# Revit family: flat_polymero_kreis_311610_002_8_19_0b9d
name_source: partatom
category: Lighting Fixtures
units: mm (PartAtom-declared; Revit-internal decimal feet)

## family parameters
Cut with Voids When Loaded = No
Host = Face
Light Source = No
Part Type = Normal
Room Calculation Point = No
Round Connector Dimension = Use Diameter
Shared = No

## types (1)
- FLAT POLYMERO KREIS (1 x LED Modul 830, 1650 lm, 3000)
    Apparent Load = 14 VA
    CIE Flux Codes = 42 73 92 86 100
    Color Rendering = 80
    Color Temperature = 3000
    Default Elevation = 1800 mm
    Description = Series: FLAT POLYMERO KREIS
Decorative round surface-mounted luminaire. Base: metal, powder-coated. Diffuser made of plastic (polycarbonate), opal, shockproof. Diffuser fastening: patented push system. Suitable for Ceiling mounting, Wall (surface). With integrated HF movement sensor. Functional parameters of the motion detector (ceiling mounting up to 4.0 m or wall mounting up to 2.7 m): HF detector 5.8 GHz ISM frequency band. Sensitivity/Range: 1-8 m in diameter, adjustable from 20-100%. Time control between 10 seconds and 30 minutes, adjustable. Coverage: 120°. Can be used as master luminaire up to 800 W (ohmic load), 500 W (fluorescent lamp, LED) / 400 A, 200 µs. Suitable for outdoor use to a limited extent only, as it is sensitive to all movements. 
Colour: white
Diameter: 360 mm
Height: 87 mm
Lamp: LED
Socket: without socket
Colour temperature: 3000K
Colour rendering index (CRI): 80
System power: 14 W
Rated luminous flux: 1650 lm
Luminous efficiency: 118 lm/W
Control gear: Regulated power supply
Protection class: I
Type of protection: IP 40
    Height = 87 mm
    Lamp = 1 x LED Modul 830
    Lamp Light Flux = 1650 lm
    Lamp count = 1
    Length = 360 mm
    Lifetime = 50000 h
    Luminous efficacy = 118 lm/W
    Manufacturer = RZB
    ModVariant = No
    Model = 311610.002.8.19
    Mounting Place = Ceiling, Wall
    Mounting Type = Surface mounted
    Number of Poles = 1
    OnlyDefault = Yes
    Power Factor = 1
    Product Name = FLAT POLYMERO KREIS
    Product group = Surface mounted ceiling and wall luminaires
    ProductGroupID = 305
    Protection Class = Protection class I
    Protection Degree = IP 40
    RLX_Detail_Level = 1
    RLX_Emergency_Light_Flux = 0 lm
    RLX_Emergency_Type = 0
    RLX_Emergency_Type_DB = No
    RlxData = <blob elided: 48725 chars, md5=91cf3a1f>
    Socket = socket
    Standby Power = 0 W
    System Light Flux = 1650 lm
    System Power = 14 W
    Type Comments = Product without accessories
    Type Image = 311595.912.79.jpg
    URL = http://relux.com
    VarID = ---
    Voltage = 230 V
    Voltage Range = 220-240 V
    Weight = 0.00 kg
    Width = 0 mm  [stored 0 ft]

note: [stored X ft] marks values corroborated as IEEE doubles in the binary element streams (Revit-internal decimal feet)

## geometry (parser evidence)
native form markers: Sweep x13
no freeform markers — native parametric forms only
